# Revit family: BoelsRental_ArticulatingBoomLift_SKYJACK_SJ63AJa
name_source: partatom
category: Site
units: mm (PartAtom-declared; Revit-internal decimal feet)

## family parameters
Always vertical = Yes
Cut with Voids When Loaded = No
OmniClass Number = 23.50.85.17
OmniClass Title = Telescoping Platforms
Part Type = Normal
Round Connector Dimension = Use Diameter
Shared = No
Work Plane-Based = No

## types (1)
- SJ63AJ
    Assembly Code = E1030100
    AssetType = Movable
    AxleOscillation = 1016 mm
    BIMObjectName = BoelsRental_ArticulatingBoomLift_SKYJACK_SJ63AJ
    BoelsSubgroup = 12007 - Articulating telescopic boom lift 20m
    Capacity = 227 KG
    ClassificationName = Uniclass2015
    ClassificationValue = Pr_65_80_47_95
    Cost = 0 $
    Description = ARTICULATED BOOM LIFT, DIESEL < 19 M
    DocumentationCertificates = https://www.boels.com
    DocumentationInstallationGuide = https://www.boels.com
    DocumentationLiterature = https://www.boels.com
    DocumentationMaintenance = https://www.boels.com
    DocumentationTechnical = https://www.boels.com
    DurationUnit = Years
    Engine = 74 HP
    ExpectedLife = 0
    FuelTankCapacity = 115 L
    Gradeability = 45%
    GroundClearance = 330 mm
    HorizontalReach = 12190 mm
    HydraulicReservoir = 115 L
    IfcExportAs = IfcTransportElement
    IfcExportType = IfcTransportElementType
    InsideTurningRadius = 2210 mm
    JibLength = 1680 mm
    JibRange = +65 / -60 Degrees
    Keynote = X
    LocalFloorLoadWithRatedLoad = 1,151 kPa
    Manufacturer = Boels Rental (SKYJACK)
    ManufacturerName = Boels Rental (SKYJACK)
    Material = Steel
    MaximumNumberOfPersons = 2
    Model = Articulating Boom Lift - SJ63AJ
    ModelNumber = SJ63AJ
    ModelReference = Articulating Boom Lift
    NBSDescription = Vertical lifting platforms
    NBSObjectName = Boels Rental - Vertical lifting platforms
    NBSReference = 90-80-65/350
    NominalDepth = 0 mm  [stored 0 ft]
    NominalHeight = 0 mm  [stored 0 ft]
    NominalLength = 0 mm  [stored 0 ft]
    OutsideTurningRadius = 5310
    OverallFloorLoadWithRatedLoad = 11.73 kPa
    OverallHeight = 2540 mm
    OverallLength = 9140 mm
    OverallWidth = 2440 mm  [stored 8.00525 ft]
    PlatformHeight = 19380 mm
    PlatformRotation = 170 Degrees
    PlatformSize = 910 mm x 2400 mm
    ProductPageLink = https://www.boels.com
    ProductionYear = 2022
    Rotation = 360 Degrees
    Size = 9140mm (L) x 2440mm (W) x 2540mm (H)
    Tailswing = 0 mm  [stored 0 ft]
    TireSize = 10.5 x 17.5
    TireType = Grip lug air-filled
    Type Comments = Articulating Boom Lift - SJ63AJ
    TypeName = Articulating Boom Lift - SJ63AJ
    URL = https://www.boels.com
    UpAndOverHeight = 8380 mm
    WarrantyDurationLabor = 0
    WarrantyDurationParts = 0
    WarrantyDurationUnit = Years
    WarrantyGuarantorLabor = https://www.boels.com
    WarrantyGuarantorParts = https://www.boels.com
    Weight = 9,616 KG
    Wheelbase = 2440 mm  [stored 8.00525 ft]
    WorkingHeight = 21210 mm
    _BSBibleVersion = 16
    _BimSpecGuid = 0
    _CurrentRevision = 1
    _DistributedBy = https://www.boels.com
    _ObjectUserGuide = https://www.boels.com

note: [stored X ft] marks values corroborated as IEEE doubles in the binary element streams (Revit-internal decimal feet)

## geometry (parser evidence)
native form markers: Sweep x47
no freeform markers — native parametric forms only
